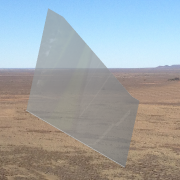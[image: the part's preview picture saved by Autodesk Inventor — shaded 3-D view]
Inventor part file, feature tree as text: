
AUTODESK INVENTOR PART (.ipt)
format: ipt  version: 2013 SP2 (Build 170200200, 200)  size: 199,168 bytes
history: native  units: in
note: dims shown in document units (in); Inventor stores cm internally (conversion verified against a paired STEP export)
features: extrude x5, sketch x5, other x4, loft x1
ambient origin geometry x8: Origin, YZ Plane, XZ Plane, XY Plane, X Axis, Y Axis, Z Axis, Center Point
bodies: Solid1 (feature_tree)
feature tree (15):
  extrude  "base"  Depth=1.0in
  other  "right"
  extrude  "upRight"  Depth=0.0481in
  extrude  "outRight"  Depth=10.0in
  other  "left"
  extrude  "upLeft"  TaperAngle=30.0deg  [1 undecoded]
  extrude  "outLeft"  Depth=0.25in
  loft  "Loft3"
  sketch  "Sketch1"  dims[d0=136.0in d1=1.0in]
  sketch  "Sketch7"  dims[d2=0.25in d3=0.0in d4=0.0481in]
  sketch  "Sketch8"  dims[d34=80.0in d35=0.0in d36=10.0in]
  sketch  "Sketch9"  dims[d37=0.25in d38=0.0in d39=30.0deg]
  sketch  "Sketch10"  dims[d40=0.5in d41=0.25in d42=100.0in d43=0.0in d44=20.0in d45=0.25in d46=0.0in d47=0.0in d48=90.0deg d49=0.0in d50=90.0deg]
  other  "Edges5"
  other  "Edges6"
note: 1 required parameter value undecoded (feature->parameter linkage not recoverable at this tier; creation-order binding heuristic only, values carry confidence <= 0.55)
